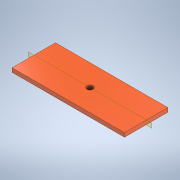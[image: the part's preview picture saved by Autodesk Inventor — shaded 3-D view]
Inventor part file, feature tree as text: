
AUTODESK INVENTOR PART (.ipt)
format: ipt  version: 2021.1 (Build 251245010, 245A)  size: 104,448 bytes
history: native  units: in
note: dims shown in document units (in); Inventor stores cm internally (conversion verified against a paired STEP export)
features: extrude x2, sketch x2
ambient origin geometry x8: Origin, YZ Plane, XZ Plane, XY Plane, X Axis, Y Axis, Z Axis, Center Point
bodies: Solid1 (feature_tree)
feature tree (4):
  extrude  "Extrusion1"  Depth=2.7in
  extrude  "Extrusion2"  Depth=0.25in
  sketch  "Sketch1"  dims[d0=7.0in d1=2.7in]
  sketch  "Sketch2"  dims[d2=0.25in d3=0.0in d4=0.375in d5=0.0in d6=0.0in]
